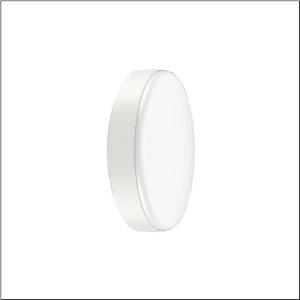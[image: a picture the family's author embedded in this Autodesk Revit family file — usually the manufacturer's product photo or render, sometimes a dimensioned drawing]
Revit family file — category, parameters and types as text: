
# Revit family: round_31_51wc10db44as
name_source: partatom
category: Lighting Fixtures
units: mm (PartAtom-declared; Revit-internal decimal feet)

## family parameters
Cut with Voids When Loaded = No
Host = Face
Light Source = No
Part Type = Normal
Room Calculation Point = No
Round Connector Dimension = Use Diameter
Shared = No

## types (1)
- Round 31 (1 x LED, 4400 lm, 35.5 W, 4000K)
    Apparent Load = 36 VA
    CIE Flux Codes = 44 75 94 94 100
    Color Rendering = 80
    Color Temperature = 4000K
    Default Elevation = 1800 mm
    Description = Round 31, wall and ceiling luminaire, primary optical cover: cover, of PC, opal, light emission: direct distribution, primary light characteristic: symmetric, installation type: surface-mounted, LED, rated luminous flux: 4.400lm, luminous efficacy: 124lm/W, light colour: 840, colour temperature: 4000K, control gear: DALI 2, with terminal, 3-pole, max. 2.5mm², mains connection: 220..240V, AC, 50/60Hz, rated input power: 35.5W, luminaire housing, of PC, traffic white (RAL 9016), diameter: 480mm, brightness and presence sensor, HF sensor, protection rating (complete): IP65, insulation class (complete): insulation class II (safety insulation), certification: CE, impact resistance: IK10, permissible operating ambient temperature: -20..+40°C, permissible storage temperature: -20..+60°C, packaging unit: 1 piece
    Height = 97 mm
    Lamp = 1 x LED
    Lamp Light Flux = 4400 lm
    Lamp Power = 35.5 W
    Lamp count = 1
    Length = 480 mm
    Luminous efficacy = 124 lm/W
    Manufacturer = Siteco
    ModVariant = No
    Model = 51WC10DB44AS
    Mounting Place = Wall
    Mounting Type = Surface mounted
    Number of Poles = 1
    OnlyDefault = Yes
    Power Factor = 1
    Product Name = Round 31
    Product group = wall and ceiling luminaire | wall mounted
    ProductGroupID = 2001
    Protection Class = Protection class II
    Protection Degree = IP 65
    RLX_Detail_Level = 1
    RLX_Emergency_Light_Flux = 0 lm
    RLX_Emergency_Type = 0
    RLX_Emergency_Type_DB = No
    RlxData = <blob elided: 40917 chars, md5=5e5ad44a>
    Socket = socket
    Standby Power = 0 W
    System Light Flux = 4400 lm
    System Power = 36 W
    Type Comments = Product without accessories
    Type Image = l_1007188.jpg
    URL = http://relux.com
    VarID = ---
    Voltage = 0 V
    Weight = 0.00 kg
    Width = 0 mm  [stored 0 ft]

note: [stored X ft] marks values corroborated as IEEE doubles in the binary element streams (Revit-internal decimal feet)

## geometry (parser evidence)
native form markers: Blend x4, Sweep x14
no freeform markers — native parametric forms only
